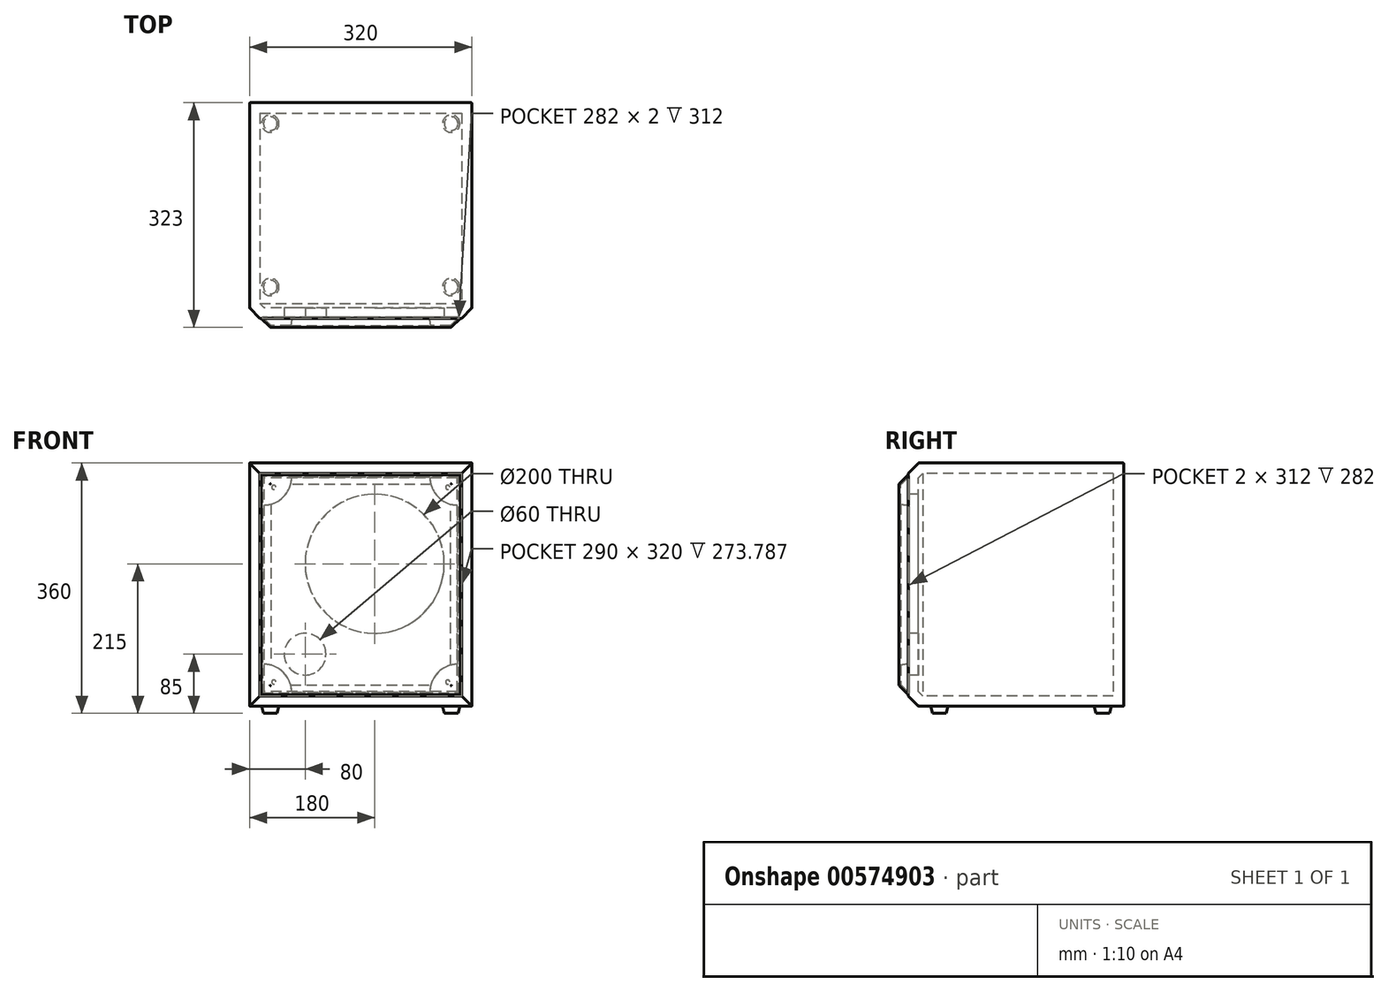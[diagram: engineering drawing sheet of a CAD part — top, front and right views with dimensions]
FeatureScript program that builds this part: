
annotation { "Feature Type Name" : "Feature", "Feature Type Description" : "" }
export const myFeature = defineFeature(function(context is Context, id is Id, definition is map)
    precondition{}
    {
        {
            var Q0;
            Q0=qCreatedBy(makeId("Top.planeOp"),FACE);
            var sketch = newSketch(context, id + "F0", { "sketchPlane" : qUnion([Q0])});
            skLineSegment(sketch, "E0.bottom", {"start": v(-160, 155) * mm, "end": v(160, 155) * mm});
            skLineSegment(sketch, "E0.top", {"start": v(-160, -155) * mm, "end": v(160, -155) * mm});
            skLineSegment(sketch, "E0.left", {"start": v(-160, 155) * mm, "end": v(-160, -155) * mm});
            skLineSegment(sketch, "E0.right", {"start": v(160, 155) * mm, "end": v(160, -155) * mm});
            skPoint(sketch, "E0.middle", {"position": v(0, 0) * mm});
            skSolve(sketch);
        }
        {
            var Q0;
            Q0 = qSketchRegion(id + "F0", true);
            extrude(context, id + "F1", {"entities" : qUnion([Q0]), "depth" : 350 * mm, "offsetDistance" : 25 * mm});
        }
        {
            var Q0;
            Q0=makeQuery(id+"F1.opExtrude","CAP_EDGE",EDGE,{"disambiguationData":[OSD([sQuery(id+"F0.wireOp",EDGE,"E0.top")])],"isStart":false});
            var Q1;
            Q1=makeQuery(id+"F1.opExtrude","SWEPT_EDGE",EDGE,{"disambiguationData":[OSD([sQuery(id+"F0.wireOp",EDGE,"E0.top"),sQuery(id+"F0.wireOp",EDGE,"E0.right")])]});
            var Q2;
            Q2=makeQuery(id+"F1.opExtrude","SWEPT_EDGE",EDGE,{"disambiguationData":[OSD([sQuery(id+"F0.wireOp",EDGE,"E0.top"),sQuery(id+"F0.wireOp",EDGE,"E0.left")])]});
            var Q3;
            Q3=makeQuery(id+"F1.opExtrude","CAP_EDGE",EDGE,{"disambiguationData":[OSD([sQuery(id+"F0.wireOp",EDGE,"E0.top")])],"isStart":true});
            chamfer(context, id + "F2", {"entities" : qUnion([Q0, Q1, Q2, Q3]), "width" : 15 * mm, "tangentPropagation" : true});
        }
        {
            var Q0;
            Q0=makeQuery(id+"F1.opExtrude","CAP_FACE",FACE,{"disambiguationData":[OSD([sQuery(id+"F0.wireOp",EDGE,"E0.bottom"),sQuery(id+"F0.wireOp",EDGE,"E0.top"),sQuery(id+"F0.wireOp",EDGE,"E0.left"),sQuery(id+"F0.wireOp",EDGE,"E0.right")])],"isStart":false});
            var Q1;
            Q1=makeQuery(id+"F1.opExtrude","SWEPT_BODY",BODY,{"disambiguationData":[OSD([sQuery(id+"F0.wireOp",EDGE,"E0.bottom"),sQuery(id+"F0.wireOp",EDGE,"E0.top"),sQuery(id+"F0.wireOp",EDGE,"E0.left"),sQuery(id+"F0.wireOp",EDGE,"E0.right")])]});
            shell(context, id + "F3", {"isHollow" : true, "entities" : qUnion([Q0]), "parts" : qUnion([Q1]), "thickness" : 15 * mm});
        }
        {
            var Q0;
            Q0=makeQuery(id+"F1.opExtrude","SWEPT_FACE",FACE,{"disambiguationData":[OSD([sQuery(id+"F0.wireOp",EDGE,"E0.top")])]});
            var sketch = newSketch(context, id + "F4", { "sketchPlane" : qUnion([Q0])});
            skCircle(sketch, "E1", {"center": v(20, 205) * mm, "radius": 100 * mm});
            skCircle(sketch, "E2", {"center": v(-80, 75) * mm, "radius": 30 * mm});
            skCircle(sketch, "E3", {"center": v(-125, 315) * mm, "radius": 3 * mm});
            skCircle(sketch, "E4", {"center": v(125, 315) * mm, "radius": 3 * mm});
            skCircle(sketch, "E5", {"center": v(125, 35) * mm, "radius": 3 * mm});
            skCircle(sketch, "E6", {"center": v(-125, 35) * mm, "radius": 3 * mm});
            skLineSegment(sketch, "E7", {"start": v(0, 335) * mm, "end": v(0, 15) * mm, "construction": true});
            skLineSegment(sketch, "E8", {"start": v(-145, 175) * mm, "end": v(145, 175) * mm, "construction": true});
            skSolve(sketch);
        }
        {
            var Q0;
            Q0=makeQuery(id+"F4.imprint","IMPRINT",FACE,{"disambiguationData":[TD([[makeQuery(id+"F4.imprint","IMPRINT",EDGE,{"derivedFrom":sQuery(id+"F4.wireOp",EDGE,"E1")}),1.0]])]});
            var Q1;
            Q1=makeQuery(id+"F4.imprint","IMPRINT",FACE,{"disambiguationData":[TD([[makeQuery(id+"F4.imprint","IMPRINT",EDGE,{"derivedFrom":sQuery(id+"F4.wireOp",EDGE,"E2")}),1.0]])]});
            extrude(context, id + "F5", {"entities" : qUnion([Q0, Q1]), "operationType" : NewBodyOperationType.REMOVE, "endBound" : BoundingType.UP_TO_NEXT, "oppositeDirection" : true, "depth" : 25 * mm, "offsetDistance" : 25 * mm});
        }
        {
            var Q0;
            Q0=makeQuery(id+"F4.imprint","IMPRINT",FACE,{"disambiguationData":[TD([[makeQuery(id+"F4.imprint","IMPRINT",EDGE,{"derivedFrom":sQuery(id+"F4.wireOp",EDGE,"E3")}),1.0]])]});
            var Q1;
            Q1=makeQuery(id+"F4.imprint","IMPRINT",FACE,{"disambiguationData":[TD([[makeQuery(id+"F4.imprint","IMPRINT",EDGE,{"derivedFrom":sQuery(id+"F4.wireOp",EDGE,"E4")}),1.0]])]});
            var Q2;
            Q2=makeQuery(id+"F4.imprint","IMPRINT",FACE,{"disambiguationData":[TD([[makeQuery(id+"F4.imprint","IMPRINT",EDGE,{"derivedFrom":sQuery(id+"F4.wireOp",EDGE,"E5")}),1.0]])]});
            var Q3;
            Q3=makeQuery(id+"F4.imprint","IMPRINT",FACE,{"disambiguationData":[TD([[makeQuery(id+"F4.imprint","IMPRINT",EDGE,{"derivedFrom":sQuery(id+"F4.wireOp",EDGE,"E6")}),1.0]])]});
            extrude(context, id + "F6", {"entities" : qUnion([Q0, Q1, Q2, Q3]), "operationType" : NewBodyOperationType.REMOVE, "oppositeDirection" : true, "depth" : 10 * mm, "offsetDistance" : 25 * mm});
        }
        {
            var Q0;
            Q0=makeQuery(id+"F1.opExtrude","SWEPT_FACE",FACE,{"disambiguationData":[OSD([sQuery(id+"F0.wireOp",EDGE,"E0.right")])]});
            fillet(context, id + "F7", {"entities" : qUnion([Q0]), "radius" : 1 * mm, "tangentPropagation" : true, "allowEdgeOverflow" : false});
        }
        {
            var Q0;
            Q0=makeQuery(id+"F1.opExtrude","SWEPT_FACE",FACE,{"disambiguationData":[OSD([sQuery(id+"F0.wireOp",EDGE,"E0.left")])]});
            var Q1;
            Q1=makeQuery(id+"F1.opExtrude","SWEPT_FACE",FACE,{"disambiguationData":[OSD([sQuery(id+"F0.wireOp",EDGE,"E0.bottom")])]});
            fillet(context, id + "F8", {"entities" : qUnion([Q0, Q1]), "radius" : 1 * mm, "tangentPropagation" : true, "allowEdgeOverflow" : false});
        }
        {
            var Q0;
            Q0=makeQuery(id+"F1.opExtrude","CAP_FACE",FACE,{"disambiguationData":[OSD([sQuery(id+"F0.wireOp",EDGE,"E0.bottom"),sQuery(id+"F0.wireOp",EDGE,"E0.top"),sQuery(id+"F0.wireOp",EDGE,"E0.left"),sQuery(id+"F0.wireOp",EDGE,"E0.right")])],"isStart":true});
            fillet(context, id + "F9", {"entities" : qUnion([Q0]), "radius" : 1 * mm, "tangentPropagation" : true, "allowEdgeOverflow" : false});
        }
        {
            var Q0;
            Q0=makeQuery(id+"F1.opExtrude","CAP_FACE",FACE,{"disambiguationData":[OSD([sQuery(id+"F0.wireOp",EDGE,"E0.bottom"),sQuery(id+"F0.wireOp",EDGE,"E0.top"),sQuery(id+"F0.wireOp",EDGE,"E0.left"),sQuery(id+"F0.wireOp",EDGE,"E0.right")])],"isStart":false});
            fillet(context, id + "F10", {"entities" : qUnion([Q0]), "radius" : 1 * mm, "tangentPropagation" : true, "allowEdgeOverflow" : false});
        }
        {
            var Q0;
            Q0=makeQuery(id+"F4.imprint","IMPRINT",FACE,{"disambiguationData":[TD([[makeQuery(id+"F4.imprint","IMPRINT",EDGE,{"derivedFrom":sQuery(id+"F4.wireOp",EDGE,"E1")}),-1.0]])]});
            var sketch = newSketch(context, id + "F11", { "sketchPlane" : qUnion([Q0])});
            skLineSegment(sketch, "E9.0", {"start": v(141, 331) * mm, "end": v(-141, 331) * mm});
            skLineSegment(sketch, "E9.1", {"start": v(141, 19) * mm, "end": v(141, 331) * mm});
            skLineSegment(sketch, "E9.2", {"start": v(-141, 19) * mm, "end": v(141, 19) * mm});
            skLineSegment(sketch, "E9.3", {"start": v(-141, 331) * mm, "end": v(-141, 19) * mm});
            skSolve(sketch);
        }
        {
            var Q0;
            Q0 = qSketchRegion(id + "F11", true);
            extrude(context, id + "F12", {"entities" : qUnion([Q0]), "operationType" : NewBodyOperationType.REMOVE, "oppositeDirection" : true, "depth" : 4 * mm, "offsetDistance" : 25 * mm});
        }
        {
            var Q0;
            Q0=makeQuery(id+"F12.boolean.opBoolean","COPY",FACE,{"derivedFrom":makeQuery(id+"F12.opExtrude","CAP_FACE",FACE,{"disambiguationData":[OSD([sQuery(id+"F11.wireOp",EDGE,"E9.0"),sQuery(id+"F11.wireOp",EDGE,"E9.1"),sQuery(id+"F11.wireOp",EDGE,"E9.2"),sQuery(id+"F11.wireOp",EDGE,"E9.3")])],"isStart":false})});
            var sketch = newSketch(context, id + "F13", { "sketchPlane" : qUnion([Q0])});
            skLineSegment(sketch, "E10.0", {"start": v(141, 331) * mm, "end": v(-141, 331) * mm});
            skLineSegment(sketch, "E11.0", {"start": v(-141, 331) * mm, "end": v(-141, 19) * mm});
            skLineSegment(sketch, "E12.0", {"start": v(141, 19) * mm, "end": v(141, 331) * mm});
            skCircle(sketch, "E13.0", {"center": v(20, 205) * mm, "radius": 100 * mm});
            skCircle(sketch, "E14.0", {"center": v(125, 315) * mm, "radius": 3 * mm});
            skCircle(sketch, "E15.0", {"center": v(125, 35) * mm, "radius": 3 * mm});
            skCircle(sketch, "E16.0", {"center": v(-125, 35) * mm, "radius": 3 * mm});
            skCircle(sketch, "E17.0", {"center": v(-125, 315) * mm, "radius": 3 * mm});
            skSolve(sketch);
        }
        {
            var Q0;
            Q0=makeQuery(id+"F13.imprint","IMPRINT",FACE,{"disambiguationData":[TD([[makeQuery(id+"F13.imprint","IMPRINT",EDGE,{"derivedFrom":sQuery(id+"F13.wireOp",EDGE,"E10.0")}),1.0]])]});
            extrude(context, id + "F14", {"entities" : qUnion([Q0]), "depth" : 2 * mm, "offsetDistance" : 25 * mm});
        }
        {
            var Q0;
            Q0=makeQuery(id+"F4.imprint","IMPRINT",FACE,{"disambiguationData":[TD([[makeQuery(id+"F4.imprint","IMPRINT",EDGE,{"derivedFrom":sQuery(id+"F4.wireOp",EDGE,"E1")}),-1.0]])]});
            var sketch = newSketch(context, id + "F15", { "sketchPlane" : qUnion([Q0])});
            skLineSegment(sketch, "E18.0", {"start": v(143, 333) * mm, "end": v(-143, 333) * mm});
            skLineSegment(sketch, "E18.1", {"start": v(143, 17) * mm, "end": v(143, 333) * mm});
            skLineSegment(sketch, "E18.2", {"start": v(-143, 17) * mm, "end": v(143, 17) * mm});
            skLineSegment(sketch, "E18.3", {"start": v(-143, 333) * mm, "end": v(-143, 17) * mm});
            skSolve(sketch);
        }
        {
            var Q0;
            Q0 = qSketchRegion(id + "F15", true);
            extrude(context, id + "F16", {"entities" : qUnion([Q0]), "depth" : 13 * mm, "offsetDistance" : 25 * mm});
        }
        {
            var Q0;
            Q0=makeQuery(id+"F16.opExtrude","CAP_EDGE",EDGE,{"disambiguationData":[OSD([sQuery(id+"F15.wireOp",EDGE,"E18.0")])],"isStart":false});
            var Q1;
            Q1=makeQuery(id+"F16.opExtrude","CAP_FACE",FACE,{"disambiguationData":[OSD([sQuery(id+"F15.wireOp",EDGE,"E18.0"),sQuery(id+"F15.wireOp",EDGE,"E18.1"),sQuery(id+"F15.wireOp",EDGE,"E18.2"),sQuery(id+"F15.wireOp",EDGE,"E18.3")])],"isStart":false});
            chamfer(context, id + "F17", {"entities" : qUnion([Q0, Q1]), "width" : 13 * mm, "tangentPropagation" : true});
        }
        {
            var Q0;
            Q0=makeQuery(id+"F4.imprint","IMPRINT",FACE,{"disambiguationData":[TD([[makeQuery(id+"F4.imprint","IMPRINT",EDGE,{"derivedFrom":sQuery(id+"F4.wireOp",EDGE,"E1")}),-1.0]])]});
            var sketch = newSketch(context, id + "F18", { "sketchPlane" : qUnion([Q0])});
            skSolve(sketch);
        }
        {
            var Q0;
            Q0=makeQuery(id+"F16.opExtrude","CAP_FACE",FACE,{"disambiguationData":[OSD([sQuery(id+"F15.wireOp",EDGE,"E18.0"),sQuery(id+"F15.wireOp",EDGE,"E18.1"),sQuery(id+"F15.wireOp",EDGE,"E18.2"),sQuery(id+"F15.wireOp",EDGE,"E18.3")])],"isStart":true});
            shell(context, id + "F19", {"entities" : qUnion([Q0]), "thickness" : 2.5 * mm});
        }
        {
            var Q0;
            Q0=makeQuery(id+"F16.opExtrude","CAP_FACE",FACE,{"disambiguationData":[OSD([sQuery(id+"F15.wireOp",EDGE,"E18.0"),sQuery(id+"F15.wireOp",EDGE,"E18.1"),sQuery(id+"F15.wireOp",EDGE,"E18.2"),sQuery(id+"F15.wireOp",EDGE,"E18.3")])],"isStart":true});
            var sketch = newSketch(context, id + "F20", { "sketchPlane" : qUnion([Q0])});
            skLineSegment(sketch, "E19", {"start": v(0, 333) * mm, "end": v(0, 20.54) * mm, "construction": true});
            skLineSegment(sketch, "E20", {"start": v(-143, 175) * mm, "end": v(139.46, 175) * mm, "construction": true});
            skArc(sketch, "E21", {"start": v(-139.46, 289.46) * mm, "mid": v(-111.18, 301.18) * mm, "end": v(-99.46, 329.46) * mm});
            skLineSegment(sketch, "E22.0", {"start": v(-139.46, 329.46) * mm, "end": v(-99.46, 329.46) * mm});
            skLineSegment(sketch, "E23.trimOffspring", {"start": v(-139.46, 289.46) * mm, "end": v(-139.46, 329.46) * mm});
            skPoint(sketch, "E24.0.start.orphan", {"position": v(-139.46, 20.54) * mm});
            skPoint(sketch, "E25.trimOffspring.end.orphan", {"position": v(139.46, 329.46) * mm});
            skArc(sketch, "E26.MirrorCS", {"start": v(139.46, 289.46) * mm, "mid": v(111.18, 301.18) * mm, "end": v(99.46, 329.46) * mm});
            skLineSegment(sketch, "E27.MirrorCS", {"start": v(139.46, 329.46) * mm, "end": v(99.46, 329.46) * mm});
            skLineSegment(sketch, "E28.MirrorCS", {"start": v(139.46, 289.46) * mm, "end": v(139.46, 329.46) * mm});
            skLineSegment(sketch, "E29.MirrorCS", {"start": v(139.46, 60.54) * mm, "end": v(139.46, 20.54) * mm});
            skArc(sketch, "E30.MirrorCS", {"start": v(139.46, 60.54) * mm, "mid": v(111.18, 48.82) * mm, "end": v(99.46, 20.54) * mm});
            skLineSegment(sketch, "E31.MirrorCS", {"start": v(139.46, 20.54) * mm, "end": v(99.46, 20.54) * mm});
            skArc(sketch, "E32.MirrorCS", {"start": v(-139.46, 60.54) * mm, "mid": v(-111.18, 48.82) * mm, "end": v(-99.46, 20.54) * mm});
            skLineSegment(sketch, "E33.MirrorCS", {"start": v(-139.46, 20.54) * mm, "end": v(-99.46, 20.54) * mm});
            skLineSegment(sketch, "E34.MirrorCS", {"start": v(-139.46, 60.54) * mm, "end": v(-139.46, 20.54) * mm});
            skSolve(sketch);
        }
        {
            var Q0;
            Q0 = qSketchRegion(id + "F20", true);
            extrude(context, id + "F21", {"entities" : qUnion([Q0]), "operationType" : NewBodyOperationType.ADD, "endBound" : BoundingType.UP_TO_NEXT, "oppositeDirection" : true, "depth" : 25 * mm, "offsetDistance" : 25 * mm});
        }
        {
            var Q0;
            Q0=makeQuery(id+"F18.imprint","IMPRINT",FACE,{"disambiguationData":[TD([[makeQuery(id+"F18.imprint","IMPRINT",EDGE,{"derivedFrom":makeQuery(id+"F4.imprint","IMPRINT",EDGE,{"derivedFrom":sQuery(id+"F4.wireOp",EDGE,"E4")})}),1.0]])]});
            var Q1;
            Q1=makeQuery(id+"F18.imprint","IMPRINT",FACE,{"disambiguationData":[TD([[makeQuery(id+"F18.imprint","IMPRINT",EDGE,{"derivedFrom":makeQuery(id+"F4.imprint","IMPRINT",EDGE,{"derivedFrom":sQuery(id+"F4.wireOp",EDGE,"E3")})}),1.0]])]});
            var Q2;
            Q2=makeQuery(id+"F18.imprint","IMPRINT",FACE,{"disambiguationData":[TD([[makeQuery(id+"F18.imprint","IMPRINT",EDGE,{"derivedFrom":makeQuery(id+"F4.imprint","IMPRINT",EDGE,{"derivedFrom":sQuery(id+"F4.wireOp",EDGE,"E5")})}),1.0]])]});
            var Q3;
            Q3=makeQuery(id+"F18.imprint","IMPRINT",FACE,{"disambiguationData":[TD([[makeQuery(id+"F18.imprint","IMPRINT",EDGE,{"derivedFrom":makeQuery(id+"F4.imprint","IMPRINT",EDGE,{"derivedFrom":sQuery(id+"F4.wireOp",EDGE,"E6")})}),1.0]])]});
            extrude(context, id + "F22", {"entities" : qUnion([Q0, Q1, Q2, Q3]), "operationType" : NewBodyOperationType.ADD, "oppositeDirection" : true, "depth" : 10 * mm, "offsetDistance" : 25 * mm});
        }
        {
            var Q0;
            Q0=makeQuery(id+"F1.opExtrude","CAP_FACE",FACE,{"disambiguationData":[OSD([sQuery(id+"F0.wireOp",EDGE,"E0.bottom"),sQuery(id+"F0.wireOp",EDGE,"E0.top"),sQuery(id+"F0.wireOp",EDGE,"E0.left"),sQuery(id+"F0.wireOp",EDGE,"E0.right")])],"isStart":true});
            var sketch = newSketch(context, id + "F23", { "sketchPlane" : qUnion([Q0])});
            skCircle(sketch, "E35", {"center": v(-130, 110) * mm, "radius": 12.5 * mm});
            skCircle(sketch, "E36.MirrorC", {"center": v(130, 110) * mm, "radius": 12.5 * mm});
            skCircle(sketch, "E37.MirrorC", {"center": v(-130, -125) * mm, "radius": 12.5 * mm});
            skCircle(sketch, "E38.MirrorC", {"center": v(130, -125) * mm, "radius": 12.5 * mm});
            skSolve(sketch);
        }
        {
            var Q0;
            Q0 = qSketchRegion(id + "F23", true);
            extrude(context, id + "F24", {"entities" : qUnion([Q0]), "depth" : 10 * mm, "offsetDistance" : 25 * mm, "hasDraft" : true, "draftAngle" : 15 * degree, "draftPullDirection" : true});
        }
        {
            var Q0;
            Q0=makeQuery(id+"F16.opExtrude","CAP_FACE",FACE,{"disambiguationData":[OSD([sQuery(id+"F15.wireOp",EDGE,"E18.0"),sQuery(id+"F15.wireOp",EDGE,"E18.1"),sQuery(id+"F15.wireOp",EDGE,"E18.2"),sQuery(id+"F15.wireOp",EDGE,"E18.3")])],"isStart":false});
            var Q1;
            Q1=makeQuery(id+"F17.opChamfer","BLEND_EDGE",EDGE,{"blendedFrom":[makeQuery(id+"F16.opExtrude","CAP_EDGE",EDGE,{"disambiguationData":[OSD([sQuery(id+"F15.wireOp",EDGE,"E18.0")])],"isStart":false}),makeQuery(id+"F16.opExtrude","CAP_EDGE",EDGE,{"disambiguationData":[OSD([sQuery(id+"F15.wireOp",EDGE,"E18.1")])],"isStart":false})],"blendedInto":[]});
            var Q2;
            Q2=makeQuery(id+"F17.opChamfer","BLEND_EDGE",EDGE,{"blendedFrom":[makeQuery(id+"F16.opExtrude","CAP_EDGE",EDGE,{"disambiguationData":[OSD([sQuery(id+"F15.wireOp",EDGE,"E18.1")])],"isStart":false}),makeQuery(id+"F16.opExtrude","CAP_EDGE",EDGE,{"disambiguationData":[OSD([sQuery(id+"F15.wireOp",EDGE,"E18.2")])],"isStart":false})],"blendedInto":[]});
            var Q3;
            Q3=makeQuery(id+"F17.opChamfer","BLEND_EDGE",EDGE,{"blendedFrom":[makeQuery(id+"F16.opExtrude","CAP_EDGE",EDGE,{"disambiguationData":[OSD([sQuery(id+"F15.wireOp",EDGE,"E18.2")])],"isStart":false}),makeQuery(id+"F16.opExtrude","CAP_EDGE",EDGE,{"disambiguationData":[OSD([sQuery(id+"F15.wireOp",EDGE,"E18.3")])],"isStart":false})],"blendedInto":[]});
            var Q4;
            Q4=makeQuery(id+"F17.opChamfer","BLEND_EDGE",EDGE,{"blendedFrom":[makeQuery(id+"F16.opExtrude","CAP_EDGE",EDGE,{"disambiguationData":[OSD([sQuery(id+"F15.wireOp",EDGE,"E18.0")])],"isStart":false}),makeQuery(id+"F16.opExtrude","CAP_EDGE",EDGE,{"disambiguationData":[OSD([sQuery(id+"F15.wireOp",EDGE,"E18.3")])],"isStart":false})],"blendedInto":[]});
            fillet(context, id + "F25", {"entities" : qUnion([Q0, Q1, Q2, Q3, Q4]), "radius" : 2 * mm, "tangentPropagation" : true, "allowEdgeOverflow" : false});
        }
    });
